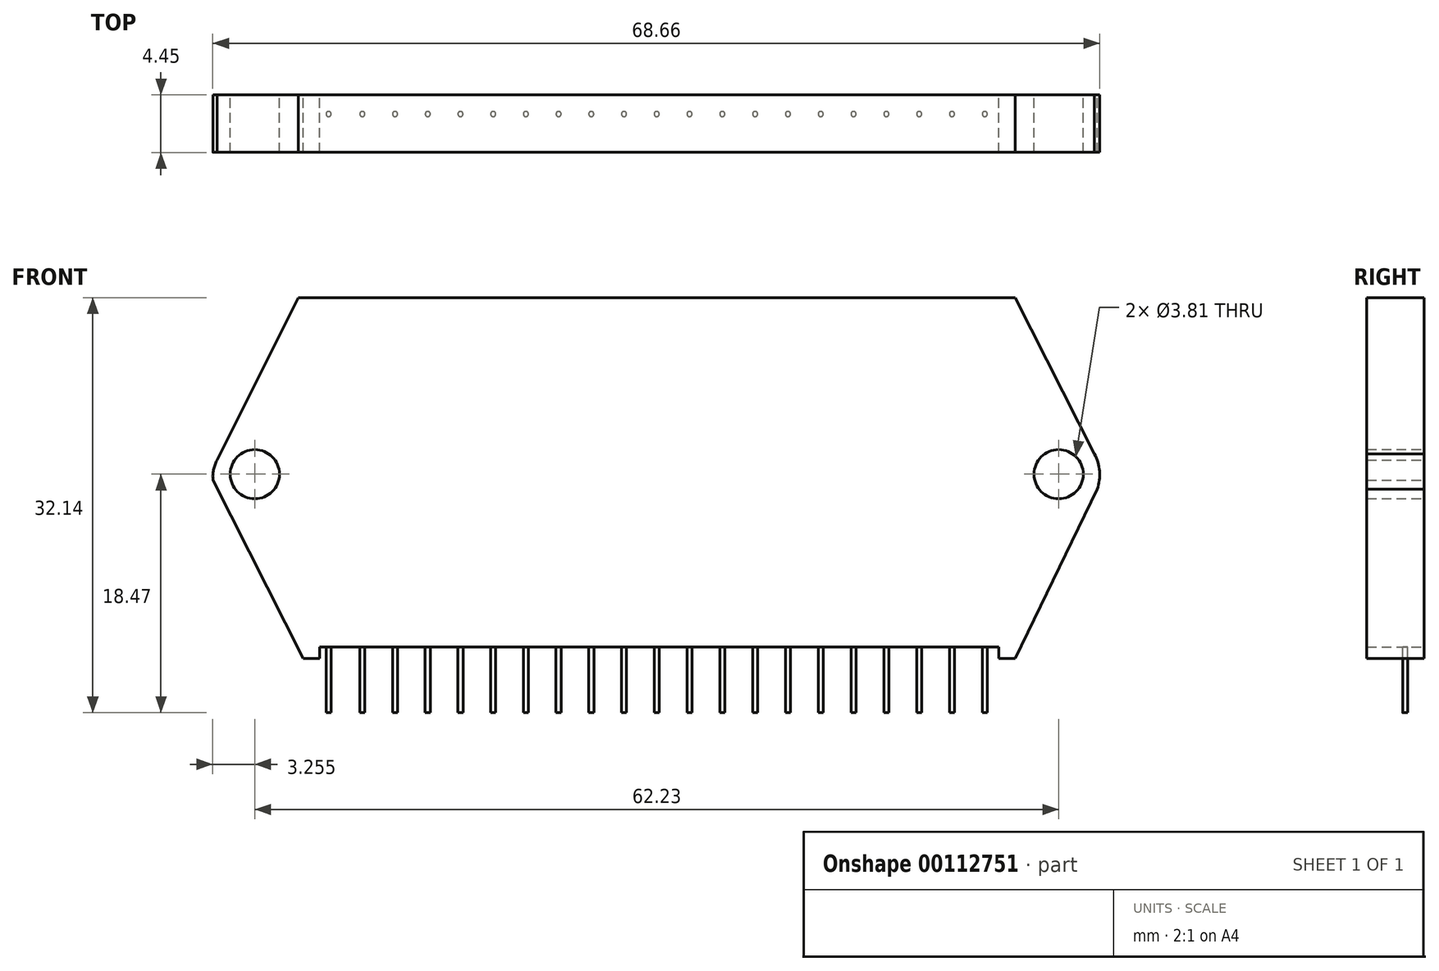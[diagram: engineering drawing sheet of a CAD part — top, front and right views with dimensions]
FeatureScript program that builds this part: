
annotation { "Feature Type Name" : "Feature", "Feature Type Description" : "" }
export const myFeature = defineFeature(function(context is Context, id is Id, definition is map)
    precondition{}
    {
        {
            var Q0;
            Q0=qCreatedBy(makeId("Front.planeOp"),FACE);
            var sketch = newSketch(context, id + "F0", { "sketchPlane" : qUnion([Q0])});
            skLineSegment(sketch, "E0.bottom", {"start": v(-27.37, -14.27) * mm, "end": v(-26.1, -14.27) * mm});
            skLineSegment(sketch, "E0.top", {"start": v(-27.76, 13.67) * mm, "end": v(27.76, 13.67) * mm});
            skLineSegment(sketch, "E0.right", {"start": v(34.3, -0.17) * mm, "end": v(34.3, 0.04) * mm});
            skCircle(sketch, "E1", {"center": v(-31.12, 0) * mm, "radius": 1.9 * mm});
            skCircle(sketch, "E2", {"center": v(31.12, 0) * mm, "radius": 1.9 * mm});
            skLineSegment(sketch, "E3", {"start": v(-27.76, 13.67) * mm, "end": v(-34.04, 1.09) * mm});
            skLineSegment(sketch, "E4", {"start": v(-34.35, -0.46) * mm, "end": v(-27.37, -14.27) * mm});
            skLineSegment(sketch, "E5", {"start": v(27.76, 13.67) * mm, "end": v(33.94, 1.46) * mm});
            skLineSegment(sketch, "E6", {"start": v(34.11, -1.17) * mm, "end": v(27.76, -14.27) * mm});
            skArc(sketch, "E7", {"start": v(34.11, -1.17) * mm, "mid": v(34.28, 0.22) * mm, "end": v(33.89, 1.57) * mm});
            skPoint(sketch, "E8.orphan", {"position": v(34.68, 0) * mm});
            skArc(sketch, "E9", {"start": v(-34.04, 1.09) * mm, "mid": v(-34.31, 0.34) * mm, "end": v(-34.35, -0.46) * mm});
            skPoint(sketch, "E10.orphan", {"position": v(-34.58, 0) * mm});
            skLineSegment(sketch, "E11", {"start": v(-26.1, -13.39) * mm, "end": v(26.5, -13.39) * mm});
            skLineSegment(sketch, "E12", {"start": v(-26.1, -14.27) * mm, "end": v(-26.1, -13.39) * mm});
            skLineSegment(sketch, "E13", {"start": v(26.5, -14.27) * mm, "end": v(26.5, -13.39) * mm});
            skLineSegment(sketch, "E14.trimOffspring", {"start": v(26.5, -14.27) * mm, "end": v(27.76, -14.27) * mm});
            skSolve(sketch);
        }
        {
            var Q0;
            Q0 = qSketchRegion(id + "F0", true);
            extrude(context, id + "F1", {"entities" : qUnion([Q0]), "depth" : 4.44 * mm});
        }
        {
            var Q0;
            Q0=makeQuery(id+"F1.opExtrude","SWEPT_FACE",FACE,{"disambiguationData":[OSD([sQuery(id+"F0.wireOp",EDGE,"E11")])]});
            var sketch = newSketch(context, id + "F2", { "sketchPlane" : qUnion([Q0])});
            skCircle(sketch, "E15", {"center": v(0, 1.47) * mm, "radius": 0.2 * mm});
            skCircle(sketch, "E16.1.0.0", {"center": v(2.54, 1.47) * mm, "radius": 0.2 * mm});
            skCircle(sketch, "E16.2.0.0", {"center": v(5.08, 1.47) * mm, "radius": 0.2 * mm});
            skCircle(sketch, "E16.3.0.0", {"center": v(7.62, 1.47) * mm, "radius": 0.2 * mm});
            skCircle(sketch, "E16.4.0.0", {"center": v(10.16, 1.47) * mm, "radius": 0.2 * mm});
            skCircle(sketch, "E16.5.0.0", {"center": v(12.7, 1.47) * mm, "radius": 0.2 * mm});
            skCircle(sketch, "E16.6.0.0", {"center": v(15.24, 1.47) * mm, "radius": 0.2 * mm});
            skCircle(sketch, "E16.7.0.0", {"center": v(17.78, 1.47) * mm, "radius": 0.2 * mm});
            skCircle(sketch, "E16.8.0.0", {"center": v(20.32, 1.47) * mm, "radius": 0.2 * mm});
            skCircle(sketch, "E16.9.0.0", {"center": v(22.86, 1.47) * mm, "radius": 0.2 * mm});
            skCircle(sketch, "E17.1.0.0", {"center": v(-2.53, 1.47) * mm, "radius": 0.2 * mm});
            skCircle(sketch, "E17.2.0.0", {"center": v(-5.06, 1.47) * mm, "radius": 0.2 * mm});
            skCircle(sketch, "E17.3.0.0", {"center": v(-7.6, 1.47) * mm, "radius": 0.2 * mm});
            skCircle(sketch, "E17.4.0.0", {"center": v(-10.13, 1.47) * mm, "radius": 0.2 * mm});
            skCircle(sketch, "E17.5.0.0", {"center": v(-12.66, 1.47) * mm, "radius": 0.2 * mm});
            skCircle(sketch, "E17.6.0.0", {"center": v(-15.2, 1.47) * mm, "radius": 0.2 * mm});
            skCircle(sketch, "E17.7.0.0", {"center": v(-17.72, 1.47) * mm, "radius": 0.2 * mm});
            skCircle(sketch, "E17.8.0.0", {"center": v(-20.26, 1.47) * mm, "radius": 0.2 * mm});
            skCircle(sketch, "E17.9.0.0", {"center": v(-22.79, 1.47) * mm, "radius": 0.2 * mm});
            skCircle(sketch, "E18.1.0.0", {"center": v(25.4, 1.47) * mm, "radius": 0.2 * mm});
            skLineSegment(sketch, "E18.direction1", {"start": v(0, 1.47) * mm, "end": v(25.4, 1.47) * mm, "construction": true});
            skCircle(sketch, "E19.1.0.0", {"center": v(-25.4, 1.47) * mm, "radius": 0.2 * mm});
            skLineSegment(sketch, "E19.direction1", {"start": v(0, 1.47) * mm, "end": v(-25.4, 1.47) * mm, "construction": true});
            skSolve(sketch);
        }
        {
            var Q0;
            Q0 = qSketchRegion(id + "F2", true);
            var Q1;
            Q1=makeQuery(id+"F2.imprint","IMPRINT",FACE,{"disambiguationData":[TD([[makeQuery(id+"F2.imprint","IMPRINT",EDGE,{"derivedFrom":sQuery(id+"F2.wireOp",EDGE,"E15")}),1.0]])]});
            var Q2;
            Q2=makeQuery(id+"F2.imprint","IMPRINT",FACE,{"disambiguationData":[TD([[makeQuery(id+"F2.imprint","IMPRINT",EDGE,{"derivedFrom":sQuery(id+"F2.wireOp",EDGE,"E17.3.0.0")}),1.0]])]});
            var Q3;
            Q3=makeQuery(id+"F2.imprint","IMPRINT",FACE,{"disambiguationData":[TD([[makeQuery(id+"F2.imprint","IMPRINT",EDGE,{"derivedFrom":sQuery(id+"F2.wireOp",EDGE,"E17.1.0.0")}),1.0]])]});
            var Q4;
            Q4=makeQuery(id+"F2.imprint","IMPRINT",FACE,{"disambiguationData":[TD([[makeQuery(id+"F2.imprint","IMPRINT",EDGE,{"derivedFrom":sQuery(id+"F2.wireOp",EDGE,"E17.2.0.0")}),1.0]])]});
            var Q5;
            Q5=makeQuery(id+"F2.imprint","IMPRINT",FACE,{"disambiguationData":[TD([[makeQuery(id+"F2.imprint","IMPRINT",EDGE,{"derivedFrom":sQuery(id+"F2.wireOp",EDGE,"E16.9.0.0")}),1.0]])]});
            var Q6;
            Q6=makeQuery(id+"F2.imprint","IMPRINT",FACE,{"disambiguationData":[TD([[makeQuery(id+"F2.imprint","IMPRINT",EDGE,{"derivedFrom":sQuery(id+"F2.wireOp",EDGE,"E16.8.0.0")}),1.0]])]});
            var Q7;
            Q7=makeQuery(id+"F2.imprint","IMPRINT",FACE,{"disambiguationData":[TD([[makeQuery(id+"F2.imprint","IMPRINT",EDGE,{"derivedFrom":sQuery(id+"F2.wireOp",EDGE,"E16.7.0.0")}),1.0]])]});
            var Q8;
            Q8=makeQuery(id+"F2.imprint","IMPRINT",FACE,{"disambiguationData":[TD([[makeQuery(id+"F2.imprint","IMPRINT",EDGE,{"derivedFrom":sQuery(id+"F2.wireOp",EDGE,"E16.6.0.0")}),1.0]])]});
            var Q9;
            Q9=makeQuery(id+"F2.imprint","IMPRINT",FACE,{"disambiguationData":[TD([[makeQuery(id+"F2.imprint","IMPRINT",EDGE,{"derivedFrom":sQuery(id+"F2.wireOp",EDGE,"E17.8.0.0")}),1.0]])]});
            var Q10;
            Q10=makeQuery(id+"F2.imprint","IMPRINT",FACE,{"disambiguationData":[TD([[makeQuery(id+"F2.imprint","IMPRINT",EDGE,{"derivedFrom":sQuery(id+"F2.wireOp",EDGE,"E16.5.0.0")}),1.0]])]});
            var Q11;
            Q11=makeQuery(id+"F2.imprint","IMPRINT",FACE,{"disambiguationData":[TD([[makeQuery(id+"F2.imprint","IMPRINT",EDGE,{"derivedFrom":sQuery(id+"F2.wireOp",EDGE,"E16.1.0.0")}),1.0]])]});
            var Q12;
            Q12=makeQuery(id+"F2.imprint","IMPRINT",FACE,{"disambiguationData":[TD([[makeQuery(id+"F2.imprint","IMPRINT",EDGE,{"derivedFrom":sQuery(id+"F2.wireOp",EDGE,"E16.2.0.0")}),1.0]])]});
            var Q13;
            Q13=makeQuery(id+"F2.imprint","IMPRINT",FACE,{"disambiguationData":[TD([[makeQuery(id+"F2.imprint","IMPRINT",EDGE,{"derivedFrom":sQuery(id+"F2.wireOp",EDGE,"E16.3.0.0")}),1.0]])]});
            var Q14;
            Q14=makeQuery(id+"F2.imprint","IMPRINT",FACE,{"disambiguationData":[TD([[makeQuery(id+"F2.imprint","IMPRINT",EDGE,{"derivedFrom":sQuery(id+"F2.wireOp",EDGE,"E16.4.0.0")}),1.0]])]});
            var Q15;
            Q15=makeQuery(id+"F2.imprint","IMPRINT",FACE,{"disambiguationData":[TD([[makeQuery(id+"F2.imprint","IMPRINT",EDGE,{"derivedFrom":sQuery(id+"F2.wireOp",EDGE,"E17.7.0.0")}),1.0]])]});
            var Q16;
            Q16=makeQuery(id+"F2.imprint","IMPRINT",FACE,{"disambiguationData":[TD([[makeQuery(id+"F2.imprint","IMPRINT",EDGE,{"derivedFrom":sQuery(id+"F2.wireOp",EDGE,"E17.9.0.0")}),1.0]])]});
            var Q17;
            Q17=makeQuery(id+"F2.imprint","IMPRINT",FACE,{"disambiguationData":[TD([[makeQuery(id+"F2.imprint","IMPRINT",EDGE,{"derivedFrom":sQuery(id+"F2.wireOp",EDGE,"E17.5.0.0")}),1.0]])]});
            var Q18;
            Q18=makeQuery(id+"F2.imprint","IMPRINT",FACE,{"disambiguationData":[TD([[makeQuery(id+"F2.imprint","IMPRINT",EDGE,{"derivedFrom":sQuery(id+"F2.wireOp",EDGE,"E17.4.0.0")}),1.0]])]});
            var Q19;
            Q19=makeQuery(id+"F2.imprint","IMPRINT",FACE,{"disambiguationData":[TD([[makeQuery(id+"F2.imprint","IMPRINT",EDGE,{"derivedFrom":sQuery(id+"F2.wireOp",EDGE,"E17.6.0.0")}),1.0]])]});
            extrude(context, id + "F3", {"entities" : qUnion([Q0, Q1, Q2, Q3, Q4, Q5, Q6, Q7, Q8, Q9, Q10, Q11, Q12, Q13, Q14, Q15, Q16, Q17, Q18, Q19]), "operationType" : NewBodyOperationType.ADD, "depth" : 5.08 * mm});
        }
    });
